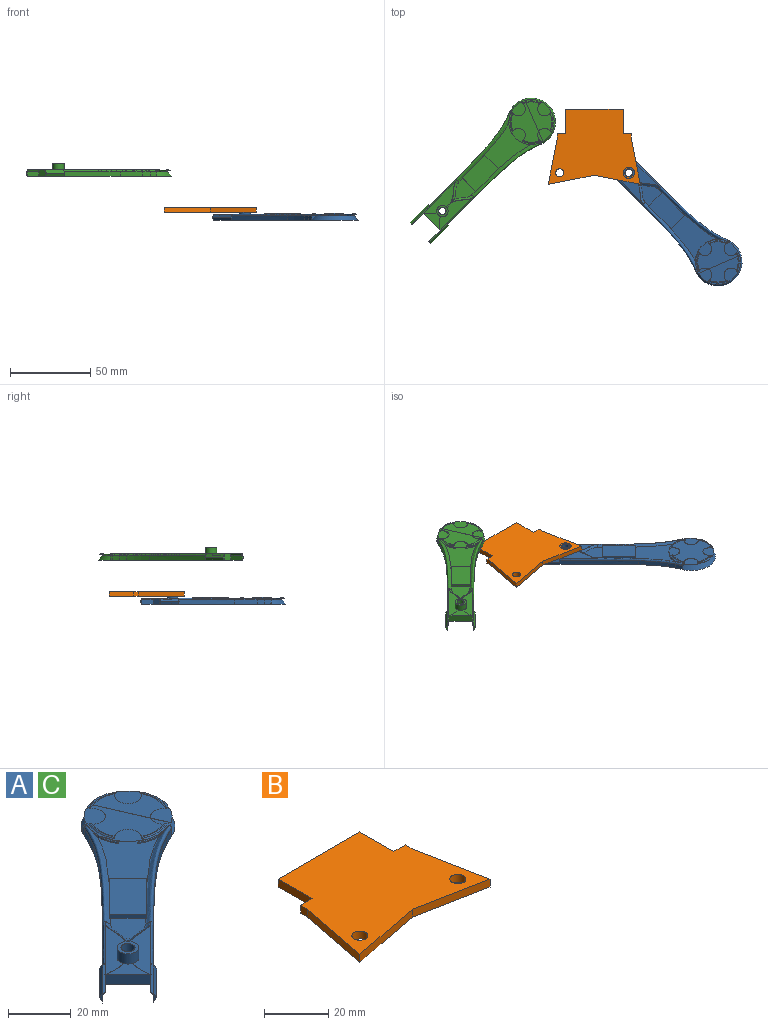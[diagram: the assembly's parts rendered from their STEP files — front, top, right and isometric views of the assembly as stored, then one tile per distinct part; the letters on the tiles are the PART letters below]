
ASSEMBLY  parts=3 mates=1
PART A: 128 faces, bbox 93.4x93.4x10.8 mm
  f0: extruded ~35.17x34.24mm, area 147.3mm2, adj f7,f9,f24,f127
  f1: extruded ~35.17x34.24mm, area 147.3mm2, adj f2,f9,f23,f120
  f2: bspline ~65.62x56.96mm, area 208.2mm2, adj f1,f3,f8,f10,f16,f17,f18,f19
  f3: bspline ~19.58x12.46mm, area 0.2mm2, adj f2,f10,f107,f108,f112
  f4: bspline ~19.58x12.46mm, area 0.1mm2, adj f6,f95,f108,f110,f112
  f5: bspline ~19.58x12.46mm, area 0.2mm2, adj f7,f10,f107,f109,f112
  f6: bspline ~19.58x12.46mm, area 0.1mm2, adj f4,f98,f109,f110,f112
  f7: bspline ~65.62x56.96mm, area 208.2mm2, adj f0,f5,f8,f10,f15,f16,f18,f24
  f8: plane 12.85x12.85mm, normal (0,0,1), area 97.2mm2, adj f2,f7,f31,f94,f96
  f9: plane 83.76x83.76mm, normal (0,0,-1), area 1900.7mm2, adj f0,f1,f10,f21,f22,f23,f24,f25
  f10: plane 11.31x11.31mm, normal (-0.71,-0.71,0), area 63.7mm2, adj f2,f3,f5,f7,f9,f107,f114,f115
  f11: plane 9.8x1.16mm, normal (0,0,1), area 2.9mm2, adj f45,f46,f48,f73,f74,f75
  f12: plane 9.8x1.16mm, normal (0,0,1), area 2.9mm2, adj f48,f50,f52,f64,f65,f66
  f13: plane 9.8x1.16mm, normal (0,0,1), area 2.9mm2, adj f49,f51,f52,f67,f68,f69
  f14: plane 6.74x6.74mm, normal (0,0,1), area 28.3mm2, adj f18,f39
  f15: plane 6.74x6.65mm, normal (0,0,1), area 28.3mm2, adj f7,f18,f40
  f16: plane 29.34x29.34mm, normal (0,0,1), area 349.9mm2, adj f2,f7,f32,f33,f34,f41,f42,f43
  f17: plane 6.74x6.65mm, normal (0,0,1), area 28.3mm2, adj f2,f18,f44
  f18: revolved ~28.75x28.72mm, area 45.6mm2, adj f2,f7,f14,f15,f17,f21,f36,f37
  f19: plane 4.29x2.09mm, normal (0,0,1), area 0.1mm2, adj f2,f21,f27,f37
  f20: plane 23x22.56mm, normal (0,0,1), area 144.6mm2, adj f29,f53,f54,f55,f56,f57,f58,f59
  f21: cylinder r=15mm len=28.87mm, axis (0,0,1), area 177mm2, adj f9,f18,f19,f26,f27,f28
  f22: extruded ~4.58x3mm, area 15.8mm2, adj f2,f9,f23,f27
  f23: extruded ~14.07x10.87mm, area 53.4mm2, adj f1,f2,f9,f22
  f24: extruded ~14.07x10.87mm, area 53.4mm2, adj f0,f7,f9,f25
  f25: extruded ~4.58x3mm, area 15.8mm2, adj f7,f9,f24,f28
  f26: plane 4.3x2.07mm, normal (0,0,1), area 0.1mm2, adj f7,f21,f28,f36
  f27: cylinder r=50mm len=3.98mm, axis (0,0,1), area 13.1mm2, adj f9,f19,f21,f22
  f28: cylinder r=50mm len=3.98mm, axis (0,0,1), area 13.1mm2, adj f7,f9,f21,f25,f26
  f29: cylinder r=4.5mm len=9mm, axis (0,0,1), area 36.8mm2, adj f20,f89
  f30: plane 6.6x6.6mm, normal (0,0,1), area 34.2mm2, adj f89
  f31: plane 8.49x8.49mm, normal (-0.71,-0.71,0), area 18mm2, adj f2,f7,f8,f32,f34,f35
  f32: plane 14.14x14.14mm, normal (0.71,-0.71,0), area 29.2mm2, adj f7,f16,f31,f33,f35
  f33: plane 8.49x8.49mm, normal (0.71,0.71,0), area 18mm2, adj f16,f32,f34,f35
  f34: plane 14.14x14.14mm, normal (-0.71,0.71,0), area 29.2mm2, adj f2,f16,f31,f33,f35
  f35: plane 22.63x22.63mm, normal (0,0,1), area 240mm2, adj f31,f32,f33,f34
  f36: plane 3.85x3.51mm, normal (-0.92,-0.4,0), area 0.1mm2, adj f7,f18,f26
  f37: plane 1.21x0.87mm, normal (-0.4,-0.92,0), area 0.1mm2, adj f2,f18,f19
  f38: plane 9.8x1.16mm, normal (0,0,1), area 2.9mm2, adj f45,f47,f49,f70,f71,f72
  f39: cylinder r=3.75mm len=7.24mm, axis (0,0,1), area 6.9mm2, adj f14,f18,f49
  f40: cylinder r=3.75mm len=7.24mm, axis (0,0,1), area 6.9mm2, adj f7,f15,f18,f52
  f41: cylinder r=14.05mm len=9.35mm, axis (0,0,1), area 4.3mm2, adj f7,f16,f42,f50
  f42: cylinder r=3.75mm len=7.46mm, axis (0,0,1), area 8.3mm2, adj f16,f41,f43,f48
  f43: cylinder r=14.05mm len=9.35mm, axis (0,0,1), area 4.3mm2, adj f2,f16,f42,f46
  f44: cylinder r=3.75mm len=7.24mm, axis (0,0,1), area 6.9mm2, adj f2,f17,f18,f45
  f45: cone r=4.95mm half-angle=50.2deg, axis (0,0,1), area 12mm2, adj f2,f11,f18,f38,f44,f46,f47,f71
  f46: cone r=12.85mm half-angle=50.2deg, axis (0,0,-1), area 18.9mm2, adj f2,f11,f43,f45,f48
  f47: cone r=12.85mm half-angle=50.2deg, axis (0,0,-1), area 14.2mm2, adj f18,f38,f45,f49
  f48: cone r=3.75mm half-angle=50.2deg, axis (0,0,1), area 12.2mm2, adj f11,f12,f42,f46,f50,f64,f65,f74
  f49: cone r=3.75mm half-angle=50.2deg, axis (0,0,1), area 12.1mm2, adj f13,f18,f38,f39,f47,f51,f68,f69
  f50: cone r=12.85mm half-angle=50.2deg, axis (0,0,-1), area 18.9mm2, adj f7,f12,f41,f48,f52
  f51: cone r=12.85mm half-angle=50.2deg, axis (0,0,-1), area 14.2mm2, adj f13,f18,f49,f52
  f52: cone r=4.95mm half-angle=50.2deg, axis (0,0,1), area 12mm2, adj f7,f12,f13,f18,f40,f50,f51,f65
  f53: extruded ~1.44x0.65mm, area 0.3mm2, adj f20,f54,f79
  f54: cone r=11.5mm half-angle=55deg, axis (0,0,-1), area 5.5mm2, adj f20,f53,f55,f79,f90
  f55: extruded ~1.44x0.65mm, area 0.3mm2, adj f20,f54,f79
  f56: extruded ~1.44x0.65mm, area 0.3mm2, adj f20,f57,f81
  f57: cone r=11.5mm half-angle=55deg, axis (0,0,-1), area 6.8mm2, adj f20,f56,f58,f81
  f58: extruded ~1.44x0.65mm, area 0.3mm2, adj f20,f57,f81
  f59: extruded ~1.44x0.65mm, area 0.3mm2, adj f20,f60,f83
  f60: cone r=11.5mm half-angle=55deg, axis (0,0,-1), area 5.5mm2, adj f20,f59,f61,f83,f92
  f61: extruded ~1.44x0.65mm, area 0.3mm2, adj f20,f60,f83
  f62: extruded ~1.44x0.65mm, area 0.3mm2, adj f20,f63,f77
  f63: cone r=11.5mm half-angle=55deg, axis (0,0,-1), area 6.8mm2, adj f20,f62,f76,f77
  f64: extruded ~0.49x0.14mm, area 0mm2, adj f12,f48,f65
  f65: cone r=12.55mm half-angle=55deg, axis (0,0,-1), area 8mm2, adj f12,f48,f52,f64,f66,f83
  f66: extruded ~0.49x0.14mm, area 0mm2, adj f12,f52,f65
  f67: extruded ~0.49x0.14mm, area 0mm2, adj f13,f52,f68
  f68: cone r=12.55mm half-angle=55deg, axis (0,0,-1), area 8mm2, adj f13,f49,f52,f67,f69,f81
  f69: extruded ~0.49x0.14mm, area 0mm2, adj f13,f49,f68
  f70: extruded ~0.49x0.14mm, area 0mm2, adj f38,f49,f71
  f71: cone r=12.55mm half-angle=55deg, axis (0,0,-1), area 8mm2, adj f38,f45,f49,f70,f72,f79
  f72: extruded ~0.49x0.14mm, area 0mm2, adj f38,f45,f71
  f73: extruded ~0.49x0.14mm, area 0mm2, adj f11,f45,f74
  f74: cone r=12.55mm half-angle=55deg, axis (0,0,-1), area 8mm2, adj f11,f45,f48,f73,f75,f77
  f75: extruded ~0.49x0.14mm, area 0mm2, adj f11,f48,f74
  f76: extruded ~1.44x0.65mm, area 0.3mm2, adj f20,f63,f77
  f77: cone r=12.11mm half-angle=35deg, axis (0,0,1), area 20.4mm2, adj f45,f48,f62,f63,f74,f76,f78,f84
  f78: cylinder r=4.3mm len=7.91mm, axis (0,0,-1), area 13.9mm2, adj f20,f45,f77,f79
  f79: cone r=12.11mm half-angle=35deg, axis (0,0,1), area 20.4mm2, adj f45,f49,f53,f54,f55,f71,f78,f80
  f80: cylinder r=4.3mm len=7.91mm, axis (0,0,-1), area 13.9mm2, adj f20,f49,f79,f81
  f81: cone r=12.11mm half-angle=35deg, axis (0,0,1), area 20.4mm2, adj f49,f52,f56,f57,f58,f68,f80,f82
  f82: cylinder r=4.3mm len=7.91mm, axis (0,0,-1), area 13.9mm2, adj f20,f52,f81,f83
  f83: cone r=12.11mm half-angle=35deg, axis (0,0,1), area 20.4mm2, adj f48,f52,f59,f60,f61,f65,f82,f84
  f84: cylinder r=4.3mm len=7.91mm, axis (0,0,-1), area 13.9mm2, adj f20,f48,f77,f83
  f85: cylinder r=2.25mm len=4.5mm, axis (0,0,1), area 32.5mm2, adj f9,f92
  f86: cylinder r=2.25mm len=4.5mm, axis (0,0,1), area 32.5mm2, adj f9,f90
  f87: cylinder r=2.25mm len=4.5mm, axis (0,0,1), area 32.5mm2, adj f9,f91
  f88: cylinder r=2.25mm len=4.5mm, axis (0,0,1), area 32.5mm2, adj f9,f93
  f89: torus R=3.3mm, axis (0,0,1), area 48.1mm2, adj f29,f30
  f90: torus R=2.95mm, axis (0,0,1), area 15mm2, adj f20,f54,f86
  f91: torus R=2.95mm, axis (0,0,1), area 17.3mm2, adj f20,f87
  f92: torus R=2.95mm, axis (0,0,1), area 15mm2, adj f20,f60,f85
  f93: torus R=2.95mm, axis (0,0,1), area 17.3mm2, adj f20,f88
  f94: bspline ~24.3x22.57mm, area 22.1mm2, adj f8,f97,f99,f102,f106
  f95: bspline ~14.57x4.15mm, area 0.4mm2, adj f2,f4,f101,f103,f108
  f96: bspline ~24.3x22.57mm, area 22.1mm2, adj f8,f97,f100,f104,f105
  f97: bspline ~2.85x2.85mm, area 1.8mm2, adj f94,f96,f102,f104
  f98: bspline ~24.12x22.4mm, area 0.4mm2, adj f6,f7,f101,f103,f109
  f99: plane 1.34x1.34mm, normal (0.71,0.71,0), area 0mm2, adj f7,f94
  f100: plane 1.32x1.32mm, normal (0.71,0.71,0), area 0mm2, adj f2,f96
  f101: bspline ~0.5x0.5mm, area 0mm2, adj f95,f98,f103
  f102: extruded ~2.16x0.96mm, area 0mm2, adj f94,f97,f103,f104,f106
  f103: plane 14.48x14.48mm, normal (0,0,1), area 2.1mm2, adj f95,f98,f101,f102,f104,f105,f106
  f104: extruded ~2.16x0.96mm, area 0mm2, adj f96,f97,f102,f103,f105
  f105: extruded ~12.14x2.93mm, area 0.1mm2, adj f96,f103,f104
  f106: extruded ~12.14x2.93mm, area 0.1mm2, adj f94,f102,f103
  f107: plane 10.52x10.52mm, normal (0,0,1), area 48.2mm2, adj f3,f5,f10,f112
  f108: plane 20.73x20.33mm, normal (0,0,1), area 120mm2, adj f2,f3,f4,f95,f112
  f109: plane 20.73x20.33mm, normal (0,0,1), area 120mm2, adj f5,f6,f7,f98,f112
  f110: plane 2.69x2.69mm, normal (0,0,1), area 2mm2, adj f4,f6,f112
  f111: cylinder r=2.25mm len=8mm, axis (0,0,-1), area 113.1mm2, adj f9,f113
  f112: cylinder r=3.5mm len=7mm, axis (0,0,-1), area 88mm2, adj f3,f4,f5,f6,f107,f108,f109,f110
  f113: plane 7x7mm, normal (0,0,1), area 22.6mm2, adj f111,f112
  f114: plane 7.07x7.07mm, normal (0.71,-0.71,0), area 30mm2, adj f10,f115,f118,f119
  f115: extruded ~7.54x7.54mm, area 13.2mm2, adj f10,f114,f116,f119
  f116: plane 11.78x11.78mm, normal (0,0,1), area 10.6mm2, adj f2,f115,f117,f119,f120
  f117: plane 12.13x12.13mm, normal (-0.61,0.61,0.5), area 37mm2, adj f116,f118,f119,f120
  f118: plane 12.17x12.13mm, normal (-0.61,0.61,-0.5), area 37mm2, adj f9,f114,f117,f119,f120
  f119: plane 4.05x1.33mm, normal (-0.71,-0.71,0), area 2.5mm2, adj f114,f115,f116,f117,f118
  f120: plane 4x1.29mm, normal (0.71,0.71,0), area 2.5mm2, adj f1,f2,f116,f117,f118
  f121: plane 7.07x7.07mm, normal (-0.71,0.71,0), area 30mm2, adj f10,f123,f124,f126
  f122: plane 11.78x11.78mm, normal (0,0,1), area 10.6mm2, adj f7,f123,f125,f126,f127
  f123: extruded ~7.54x7.54mm, area 13.2mm2, adj f10,f121,f122,f126
  f124: plane 12.13x12.13mm, normal (0.61,-0.61,-0.5), area 36.9mm2, adj f9,f121,f125,f126,f127
  f125: plane 12.13x12.13mm, normal (0.61,-0.61,0.5), area 37mm2, adj f122,f124,f126,f127
  f126: plane 4.05x1.33mm, normal (-0.71,-0.71,0), area 2.5mm2, adj f121,f122,f123,f124,f125
  f127: plane 4x1.29mm, normal (0.71,0.71,0), area 2.5mm2, adj f0,f7,f122,f124,f125
PART B: 15 faces, bbox 57.2x46.6x3 mm
  f0: plane 14.95x3mm, normal (-1,0,0), area 44.9mm2, adj f1,f11,f13,f14
  f1: plane 5x3mm, normal (0,1,0), area 15mm2, adj f0,f2,f13,f14
  f2: plane 3.05x3mm, normal (-1,0,0), area 9.1mm2, adj f1,f3,f13,f14
  f3: plane 28.61x5.61mm, normal (-0.98,0.19,0), area 87.5mm2, adj f2,f4,f13,f14
  f4: plane 28.61x5.61mm, normal (0.19,-0.98,0), area 87.5mm2, adj f3,f5,f13,f14
  f5: plane 28.61x5.61mm, normal (-0.19,-0.98,0), area 87.5mm2, adj f4,f6,f13,f14
  f6: plane 28.61x5.61mm, normal (0.98,0.19,0), area 87.5mm2, adj f5,f7,f13,f14
  f7: plane 3.05x3mm, normal (1,0,0), area 9.1mm2, adj f6,f8,f13,f14
  f8: plane 5x3mm, normal (0,1,0), area 15mm2, adj f7,f9,f13,f14
  f9: plane 14.95x3mm, normal (1,0,0), area 44.9mm2, adj f8,f11,f13,f14
  f10: cylinder r=2.5mm len=5mm, axis (0,0,-1), area 47.1mm2, adj f13,f14
  f11: plane 36x3mm, normal (0,1,0), area 108mm2, adj f0,f9,f13,f14
  f12: cylinder r=2.5mm len=5mm, axis (0,0,-1), area 47.1mm2, adj f13,f14
  f13: plane 57.21x46.61mm, normal (0,0,1), area 1955.1mm2, adj f0,f1,f2,f3,f4,f5,f6,f7
  f14: plane 57.21x46.61mm, normal (0,0,-1), area 1955.1mm2, adj f0,f1,f2,f3,f4,f5,f6,f7
PART C: same geometry as A
PLACE A rot(axis=(0,0,-1),90deg) t=(24.92,-94.05,-1.64)mm
PLACE B t=(-51.99,-17.14,0.36)mm
PLACE C t=(-91.07,-7.14,25.75)mm
MATE fastened A.f111 <-> B.f12  axis (0,0,1) through (-30.45,-38.68,3.36)mm
